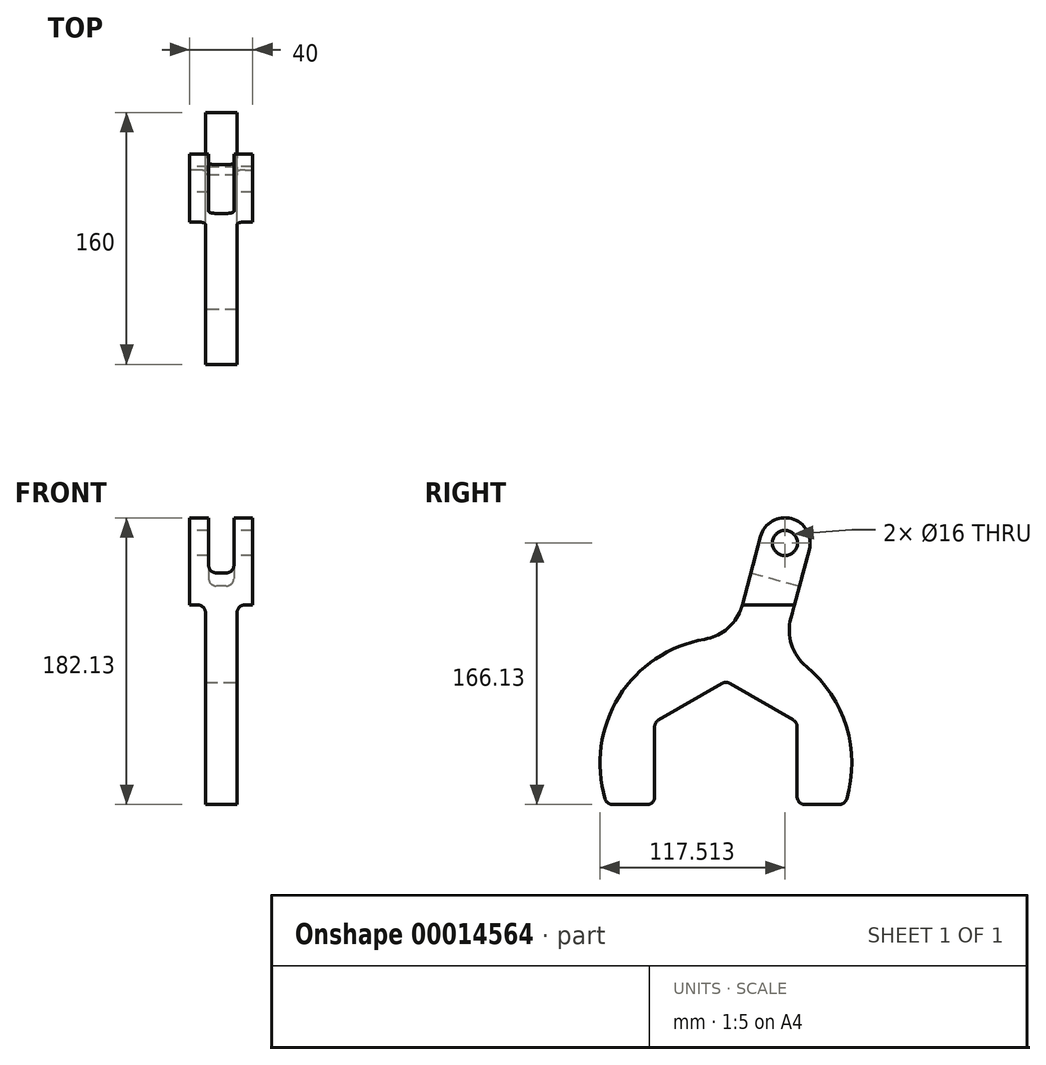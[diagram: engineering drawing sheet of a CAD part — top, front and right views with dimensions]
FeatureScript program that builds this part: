
annotation { "Feature Type Name" : "Feature", "Feature Type Description" : "" }
export const myFeature = defineFeature(function(context is Context, id is Id, definition is map)
    precondition{}
    {
        {
            var Q0;
            Q0=qCreatedBy(makeId("Right.planeOp"),FACE);
            var sketch = newSketch(context, id + "F0", { "sketchPlane" : qUnion([Q0])});
            skCircle(sketch, "E0.cCircle", {"center": v(0, 0) * mm, "radius": 45.25 * mm, "construction": true});
            skLineSegment(sketch, "E0.0", {"start": v(-45.25, -26.13) * mm, "end": v(-45.25, 26.13) * mm});
            skLineSegment(sketch, "E0.1", {"start": v(-45.25, 26.13) * mm, "end": v(0, 52.25) * mm});
            skLineSegment(sketch, "E0.2", {"start": v(0, 52.25) * mm, "end": v(45.25, 26.13) * mm});
            skLineSegment(sketch, "E0.3", {"start": v(45.25, 26.13) * mm, "end": v(45.25, -26.13) * mm});
            skLineSegment(sketch, "E0.4", {"start": v(22.63, -39.19) * mm, "end": v(21.51, -39.83) * mm});
            skPoint(sketch, "E0.0.midPoint", {"position": v(-45.25, 0) * mm});
            skLineSegment(sketch, "E1", {"start": v(0, 0) * mm, "end": v(0, 140) * mm, "construction": true});
            skLineSegment(sketch, "E2", {"start": v(0, 140) * mm, "end": v(132.53, 140) * mm, "construction": true});
            skLineSegment(sketch, "E3", {"start": v(0, 0) * mm, "end": v(37.51, 140) * mm, "construction": true});
            skCircle(sketch, "E4", {"center": v(37.51, 140) * mm, "radius": 8 * mm});
            skArc(sketch, "E5", {"start": v(75.61, -26.13) * mm, "mid": v(77.05, 21.53) * mm, "end": v(51.12, 61.53) * mm});
            skLineSegment(sketch, "E6", {"start": v(37.51, 140) * mm, "end": v(37.51, 210.9) * mm, "construction": true});
            skLineSegment(sketch, "E7", {"start": v(-75.61, -26.13) * mm, "end": v(-45.25, -26.13) * mm});
            skPoint(sketch, "E8.orphan", {"position": v(53.51, -53.76) * mm});
            skArc(sketch, "E9.trimOffspring", {"start": v(-13.5, 78.85) * mm, "mid": v(-68.85, 40.74) * mm, "end": v(-75.61, -26.13) * mm});
            skPoint(sketch, "E10.orphan", {"position": v(-113.23, -26.13) * mm});
            skLineSegment(sketch, "E11.trimOffspring", {"start": v(45.25, -26.13) * mm, "end": v(75.61, -26.13) * mm});
            skPoint(sketch, "E12.visualSharp", {"position": v(61.16, 51.57) * mm});
            skPoint(sketch, "E13.newPointA", {"position": v(21.51, -53.76) * mm});
            skLineSegment(sketch, "E14.0", {"start": v(41.32, 92.37) * mm, "end": v(52.97, 135.86) * mm});
            skCircle(sketch, "E15", {"center": v(37.51, 140) * mm, "radius": 16 * mm});
            skLineSegment(sketch, "E16.0.MirrorCS", {"start": v(10.4, 100.66) * mm, "end": v(22.06, 144.14) * mm});
            skPoint(sketch, "E17.orphan", {"position": v(-15.45, 4.14) * mm});
            skPoint(sketch, "E18.orphan", {"position": v(15.45, -4.14) * mm});
            skPoint(sketch, "E19.visualSharp", {"position": v(4.83, 79.85) * mm});
            skArc(sketch, "E19.filletArc", {"start": v(-13.5, 78.85) * mm, "mid": v(1.64, 86.25) * mm, "end": v(10.4, 100.66) * mm});
            skPoint(sketch, "E20.visualSharp", {"position": v(35.74, 71.57) * mm});
            skArc(sketch, "E20.filletArc", {"start": v(41.32, 92.37) * mm, "mid": v(41.7, 75.52) * mm, "end": v(51.12, 61.53) * mm});
            skSolve(sketch);
        }
        {
            var Q0;
            Q0=qSketchRegion(id+"F0",true);
            extrude(context, id + "F1", {"entities" : qUnion([Q0]), "endBound" : BoundingType.SYMMETRIC, "depth" : 40 * mm});
        }
        {
            var Q0;
            Q0=makeQuery(id+"F1.opExtrude","SWEPT_EDGE",EDGE,{"disambiguationData":[OSD([sQuery(id+"F0.wireOp",EDGE,"E0.3"),sQuery(id+"F0.wireOp",EDGE,"E11.trimOffspring")])]});
            var Q1;
            Q1=makeQuery(id+"F1.opExtrude","SWEPT_EDGE",EDGE,{"disambiguationData":[OSD([sQuery(id+"F0.wireOp",EDGE,"E0.0"),sQuery(id+"F0.wireOp",EDGE,"E7")])]});
            var Q2;
            Q2=makeQuery(id+"F1.opExtrude","SWEPT_EDGE",EDGE,{"disambiguationData":[OSD([sQuery(id+"F0.wireOp",EDGE,"E7"),sQuery(id+"F0.wireOp",EDGE,"E9.trimOffspring")])]});
            var Q3;
            Q3=makeQuery(id+"F1.opExtrude","SWEPT_EDGE",EDGE,{"disambiguationData":[OSD([sQuery(id+"F0.wireOp",EDGE,"E5"),sQuery(id+"F0.wireOp",EDGE,"E11.trimOffspring")])]});
            fillet(context, id + "F2", {"entities" : qUnion([Q0, Q1, Q2, Q3]), "radius" : 5 * mm, "tangentPropagation" : true, "allowEdgeOverflow" : false});
        }
        {
            var Q0;
            Q0=makeQuery(id+"F1.opExtrude","SWEPT_EDGE",EDGE,{"disambiguationData":[OSD([sQuery(id+"F0.wireOp",EDGE,"E0.2"),sQuery(id+"F0.wireOp",EDGE,"E0.3")])]});
            var Q1;
            Q1=makeQuery(id+"F1.opExtrude","SWEPT_EDGE",EDGE,{"disambiguationData":[OSD([sQuery(id+"F0.wireOp",EDGE,"E0.1"),sQuery(id+"F0.wireOp",EDGE,"E0.2")])]});
            var Q2;
            Q2=makeQuery(id+"F1.opExtrude","SWEPT_EDGE",EDGE,{"disambiguationData":[OSD([sQuery(id+"F0.wireOp",EDGE,"E0.0"),sQuery(id+"F0.wireOp",EDGE,"E0.1")])]});
            fillet(context, id + "F3", {"entities" : qUnion([Q0, Q1, Q2]), "radius" : 5 * mm, "tangentPropagation" : true, "allowEdgeOverflow" : false});
        }
        {
            var Q0;
            Q0=makeQuery(id+"F1.opExtrude","CAP_FACE",FACE,{"disambiguationData":[OSD([sQuery(id+"F0.wireOp",EDGE,"E0.0"),sQuery(id+"F0.wireOp",EDGE,"E0.1"),sQuery(id+"F0.wireOp",EDGE,"E0.2"),sQuery(id+"F0.wireOp",EDGE,"E0.3"),sQuery(id+"F0.wireOp",EDGE,"E4"),sQuery(id+"F0.wireOp",EDGE,"E5"),sQuery(id+"F0.wireOp",EDGE,"E7"),sQuery(id+"F0.wireOp",EDGE,"E9.trimOffspring"),sQuery(id+"F0.wireOp",EDGE,"E11.trimOffspring"),sQuery(id+"F0.wireOp",EDGE,"E14.0"),sQuery(id+"F0.wireOp",EDGE,"E15"),sQuery(id+"F0.wireOp",EDGE,"E16.0.MirrorCS"),sQuery(id+"F0.wireOp",EDGE,"E19.filletArc"),sQuery(id+"F0.wireOp",EDGE,"E20.filletArc")])],"isStart":false});
            var sketch = newSketch(context, id + "F4", { "sketchPlane" : qUnion([Q0])});
            skLineSegment(sketch, "E21", {"start": v(0, 0) * mm, "end": v(130.77, 0) * mm, "construction": true});
            skLineSegment(sketch, "E22", {"start": v(10.4, 100.66) * mm, "end": v(43.54, 100.66) * mm});
            skArc(sketch, "E23.0", {"start": v(-13.5, 78.85) * mm, "mid": v(1.64, 86.25) * mm, "end": v(10.4, 100.66) * mm});
            skArc(sketch, "E24.0", {"start": v(-13.5, 78.85) * mm, "mid": v(-67.87, 42.35) * mm, "end": v(-76.76, -22.53) * mm});
            skLineSegment(sketch, "E25.0.0", {"start": v(-71.96, -26.13) * mm, "end": v(-50.25, -26.13) * mm});
            skArc(sketch, "E25.0.1", {"start": v(-50.25, -26.13) * mm, "mid": v(-46.71, -24.66) * mm, "end": v(-45.25, -21.13) * mm});
            skLineSegment(sketch, "E25.0.2", {"start": v(-45.25, -21.13) * mm, "end": v(-45.25, 23.24) * mm});
            skArc(sketch, "E25.0.3", {"start": v(-45.25, 23.24) * mm, "mid": v(-44.58, 25.74) * mm, "end": v(-42.75, 27.57) * mm});
            skLineSegment(sketch, "E25.0.4", {"start": v(-42.75, 27.57) * mm, "end": v(-2.5, 50.8) * mm});
            skArc(sketch, "E25.0.5", {"start": v(-2.5, 50.8) * mm, "mid": v(0, 51.48) * mm, "end": v(2.5, 50.8) * mm});
            skLineSegment(sketch, "E25.0.6", {"start": v(2.5, 50.8) * mm, "end": v(42.75, 27.57) * mm});
            skArc(sketch, "E25.0.7", {"start": v(42.75, 27.57) * mm, "mid": v(44.58, 25.74) * mm, "end": v(45.25, 23.24) * mm});
            skLineSegment(sketch, "E25.0.8", {"start": v(45.25, 23.24) * mm, "end": v(45.25, -21.13) * mm});
            skArc(sketch, "E25.0.9", {"start": v(45.25, -21.13) * mm, "mid": v(46.71, -24.66) * mm, "end": v(50.25, -26.13) * mm});
            skLineSegment(sketch, "E25.0.10", {"start": v(50.25, -26.13) * mm, "end": v(71.96, -26.13) * mm});
            skArc(sketch, "E25.0.11", {"start": v(71.96, -26.13) * mm, "mid": v(74.96, -25.13) * mm, "end": v(76.76, -22.53) * mm});
            skArc(sketch, "E25.0.12", {"start": v(76.76, -22.53) * mm, "mid": v(76.52, 23.34) * mm, "end": v(51.12, 61.53) * mm});
            skArc(sketch, "E25.0.13", {"start": v(51.12, 61.53) * mm, "mid": v(41.7, 75.52) * mm, "end": v(41.32, 92.37) * mm});
            skLineSegment(sketch, "E25.0.14", {"start": v(41.32, 92.37) * mm, "end": v(43.54, 100.66) * mm});
            skArc(sketch, "E25.0.17", {"start": v(10.4, 100.66) * mm, "mid": v(1.64, 86.25) * mm, "end": v(-13.5, 78.85) * mm});
            skArc(sketch, "E25.0.19", {"start": v(-76.76, -22.53) * mm, "mid": v(-74.96, -25.13) * mm, "end": v(-71.96, -26.13) * mm});
            skPoint(sketch, "E25.0.15.end.orphan", {"position": v(22.06, 144.14) * mm});
            skPoint(sketch, "E26.orphan", {"position": v(52.97, 135.86) * mm});
            skSolve(sketch);
        }
        {
            var Q0;
            Q0=qSketchRegion(id+"F4",true);
            extrude(context, id + "F5", {"entities" : qUnion([Q0]), "operationType" : NewBodyOperationType.REMOVE, "oppositeDirection" : true, "depth" : 10 * mm});
        }
        {
            var Q0;
            Q0=makeQuery(id+"F1.opExtrude","CAP_FACE",FACE,{"disambiguationData":[OSD([sQuery(id+"F0.wireOp",EDGE,"E0.0"),sQuery(id+"F0.wireOp",EDGE,"E0.1"),sQuery(id+"F0.wireOp",EDGE,"E0.2"),sQuery(id+"F0.wireOp",EDGE,"E0.3"),sQuery(id+"F0.wireOp",EDGE,"E4"),sQuery(id+"F0.wireOp",EDGE,"E5"),sQuery(id+"F0.wireOp",EDGE,"E7"),sQuery(id+"F0.wireOp",EDGE,"E9.trimOffspring"),sQuery(id+"F0.wireOp",EDGE,"E11.trimOffspring"),sQuery(id+"F0.wireOp",EDGE,"E14.0"),sQuery(id+"F0.wireOp",EDGE,"E15"),sQuery(id+"F0.wireOp",EDGE,"E16.0.MirrorCS"),sQuery(id+"F0.wireOp",EDGE,"E19.filletArc"),sQuery(id+"F0.wireOp",EDGE,"E20.filletArc")])],"isStart":true});
            var sketch = newSketch(context, id + "F6", { "sketchPlane" : qUnion([Q0])});
            skLineSegment(sketch, "E27.0.0", {"start": v(45.25, 23.24) * mm, "end": v(45.25, -21.13) * mm});
            skArc(sketch, "E27.0.1", {"start": v(45.25, -21.13) * mm, "mid": v(46.71, -24.66) * mm, "end": v(50.25, -26.13) * mm});
            skLineSegment(sketch, "E27.0.2", {"start": v(50.25, -26.13) * mm, "end": v(71.96, -26.13) * mm});
            skArc(sketch, "E27.0.3", {"start": v(71.96, -26.13) * mm, "mid": v(74.96, -25.13) * mm, "end": v(76.76, -22.53) * mm});
            skArc(sketch, "E27.0.4", {"start": v(76.76, -22.53) * mm, "mid": v(67.87, 42.35) * mm, "end": v(13.5, 78.85) * mm});
            skArc(sketch, "E27.0.5", {"start": v(13.5, 78.85) * mm, "mid": v(-1.64, 86.25) * mm, "end": v(-10.4, 100.66) * mm});
            skArc(sketch, "E27.0.7", {"start": v(-22.06, 144.14) * mm, "mid": v(-41.65, 155.45) * mm, "end": v(-52.97, 135.86) * mm});
            skLineSegment(sketch, "E27.0.8", {"start": v(-43.54, 100.66) * mm, "end": v(-41.32, 92.37) * mm});
            skArc(sketch, "E27.0.9", {"start": v(-41.32, 92.37) * mm, "mid": v(-41.7, 75.52) * mm, "end": v(-51.12, 61.53) * mm});
            skArc(sketch, "E27.0.10", {"start": v(-51.12, 61.53) * mm, "mid": v(-76.52, 23.34) * mm, "end": v(-76.76, -22.53) * mm});
            skArc(sketch, "E27.0.11", {"start": v(-76.76, -22.53) * mm, "mid": v(-74.96, -25.13) * mm, "end": v(-71.96, -26.13) * mm});
            skLineSegment(sketch, "E27.0.12", {"start": v(-71.96, -26.13) * mm, "end": v(-50.25, -26.13) * mm});
            skArc(sketch, "E27.0.13", {"start": v(-50.25, -26.13) * mm, "mid": v(-46.71, -24.66) * mm, "end": v(-45.25, -21.13) * mm});
            skLineSegment(sketch, "E27.0.14", {"start": v(-45.25, -21.13) * mm, "end": v(-45.25, 23.24) * mm});
            skArc(sketch, "E27.0.15", {"start": v(-45.25, 23.24) * mm, "mid": v(-44.58, 25.74) * mm, "end": v(-42.75, 27.57) * mm});
            skLineSegment(sketch, "E27.0.16", {"start": v(-42.75, 27.57) * mm, "end": v(-2.5, 50.8) * mm});
            skArc(sketch, "E27.0.17", {"start": v(-2.5, 50.8) * mm, "mid": v(0, 51.48) * mm, "end": v(2.5, 50.8) * mm});
            skLineSegment(sketch, "E27.0.18", {"start": v(2.5, 50.8) * mm, "end": v(42.75, 27.57) * mm});
            skArc(sketch, "E27.0.19", {"start": v(42.75, 27.57) * mm, "mid": v(44.58, 25.74) * mm, "end": v(45.25, 23.24) * mm});
            skLineSegment(sketch, "E28.0", {"start": v(-10.4, 100.66) * mm, "end": v(-43.54, 100.66) * mm});
            skSolve(sketch);
        }
        {
            var Q0;
            Q0=qSketchRegion(id+"F6",true);
            extrude(context, id + "F7", {"entities" : qUnion([Q0]), "operationType" : NewBodyOperationType.REMOVE, "oppositeDirection" : true, "depth" : 10 * mm});
        }
        {
            var Q0;
            Q0=makeQuery(id+"F7.boolean.opBoolean","COPY",EDGE,{"derivedFrom":makeQuery(id+"F7.opExtrude","CAP_EDGE",EDGE,{"disambiguationData":[OSD([sQuery(id+"F6.wireOp",EDGE,"E28.0")])],"isStart":false})});
            var Q1;
            Q1=makeQuery(id+"F7.boolean.opBoolean","COPY",EDGE,{"derivedFrom":makeQuery(id+"F7.opExtrude","CAP_EDGE",EDGE,{"disambiguationData":[OSD([sQuery(id+"F6.wireOp",EDGE,"E28.0")])],"isStart":true})});
            var Q2;
            Q2=makeQuery(id+"F5.boolean.opBoolean","COPY",EDGE,{"derivedFrom":makeQuery(id+"F5.opExtrude","CAP_EDGE",EDGE,{"disambiguationData":[OSD([sQuery(id+"F4.wireOp",EDGE,"E22")])],"isStart":false})});
            var Q3;
            Q3=makeQuery(id+"F5.boolean.opBoolean","COPY",EDGE,{"derivedFrom":makeQuery(id+"F5.opExtrude","CAP_EDGE",EDGE,{"disambiguationData":[OSD([sQuery(id+"F4.wireOp",EDGE,"E22")])],"isStart":true})});
            fillet(context, id + "F8", {"entities" : qUnion([Q0, Q1, Q2, Q3]), "radius" : 5 * mm, "tangentPropagation" : true, "allowEdgeOverflow" : false});
        }
        {
            var Q0;
            Q0=makeQuery(id+"F1.opExtrude","SWEPT_FACE",FACE,{"disambiguationData":[OSD([sQuery(id+"F0.wireOp",EDGE,"E14.0")])]});
            var sketch = newSketch(context, id + "F9", { "sketchPlane" : qUnion([Q0])});
            skLineSegment(sketch, "E29.0", {"start": v(-20, 144.94) * mm, "end": v(20, 144.94) * mm, "construction": true});
            skLineSegment(sketch, "E30", {"start": v(-20, 160.94) * mm, "end": v(20, 160.94) * mm, "construction": true});
            skLineSegment(sketch, "E31.0.MirrorCS", {"start": v(-20, 128.94) * mm, "end": v(20, 128.94) * mm, "construction": true});
            skLineSegment(sketch, "E32.0", {"start": v(-20, 120.94) * mm, "end": v(20, 120.94) * mm, "construction": true});
            skLineSegment(sketch, "E33", {"start": v(0, 160.94) * mm, "end": v(0, 105.69) * mm, "construction": true});
            skLineSegment(sketch, "E34.0", {"start": v(8, 160.94) * mm, "end": v(8, 105.69) * mm, "construction": true});
            skLineSegment(sketch, "E35.0.MirrorCS", {"start": v(-8, 160.94) * mm, "end": v(-8, 105.69) * mm, "construction": true});
            skLineSegment(sketch, "E36.bottom", {"start": v(-8, 160.94) * mm, "end": v(8, 160.94) * mm});
            skLineSegment(sketch, "E36.top", {"start": v(-8, 120.94) * mm, "end": v(8, 120.94) * mm});
            skLineSegment(sketch, "E36.left", {"start": v(-8, 160.94) * mm, "end": v(-8, 120.94) * mm});
            skLineSegment(sketch, "E36.right", {"start": v(8, 160.94) * mm, "end": v(8, 120.94) * mm});
            skSolve(sketch);
        }
        {
            var Q0;
            Q0=qSketchRegion(id+"F9",true);
            extrude(context, id + "F10", {"entities" : qUnion([Q0]), "operationType" : NewBodyOperationType.REMOVE, "endBound" : BoundingType.THROUGH_ALL, "oppositeDirection" : true, "depth" : 25 * mm});
        }
        {
            var Q0;
            Q0=makeQuery(id+"F10.boolean.opBoolean","COPY",EDGE,{"derivedFrom":makeQuery(id+"F10.opExtrude","SWEPT_EDGE",EDGE,{"disambiguationData":[OSD([sQuery(id+"F9.wireOp",EDGE,"E36.top"),sQuery(id+"F9.wireOp",EDGE,"E36.left")])]})});
            var Q1;
            Q1=makeQuery(id+"F10.boolean.opBoolean","COPY",EDGE,{"derivedFrom":makeQuery(id+"F10.opExtrude","SWEPT_EDGE",EDGE,{"disambiguationData":[OSD([sQuery(id+"F9.wireOp",EDGE,"E36.top"),sQuery(id+"F9.wireOp",EDGE,"E36.right")])]})});
            fillet(context, id + "F11", {"entities" : qUnion([Q0, Q1]), "radius" : 5 * mm, "tangentPropagation" : true, "allowEdgeOverflow" : false});
        }
    });
